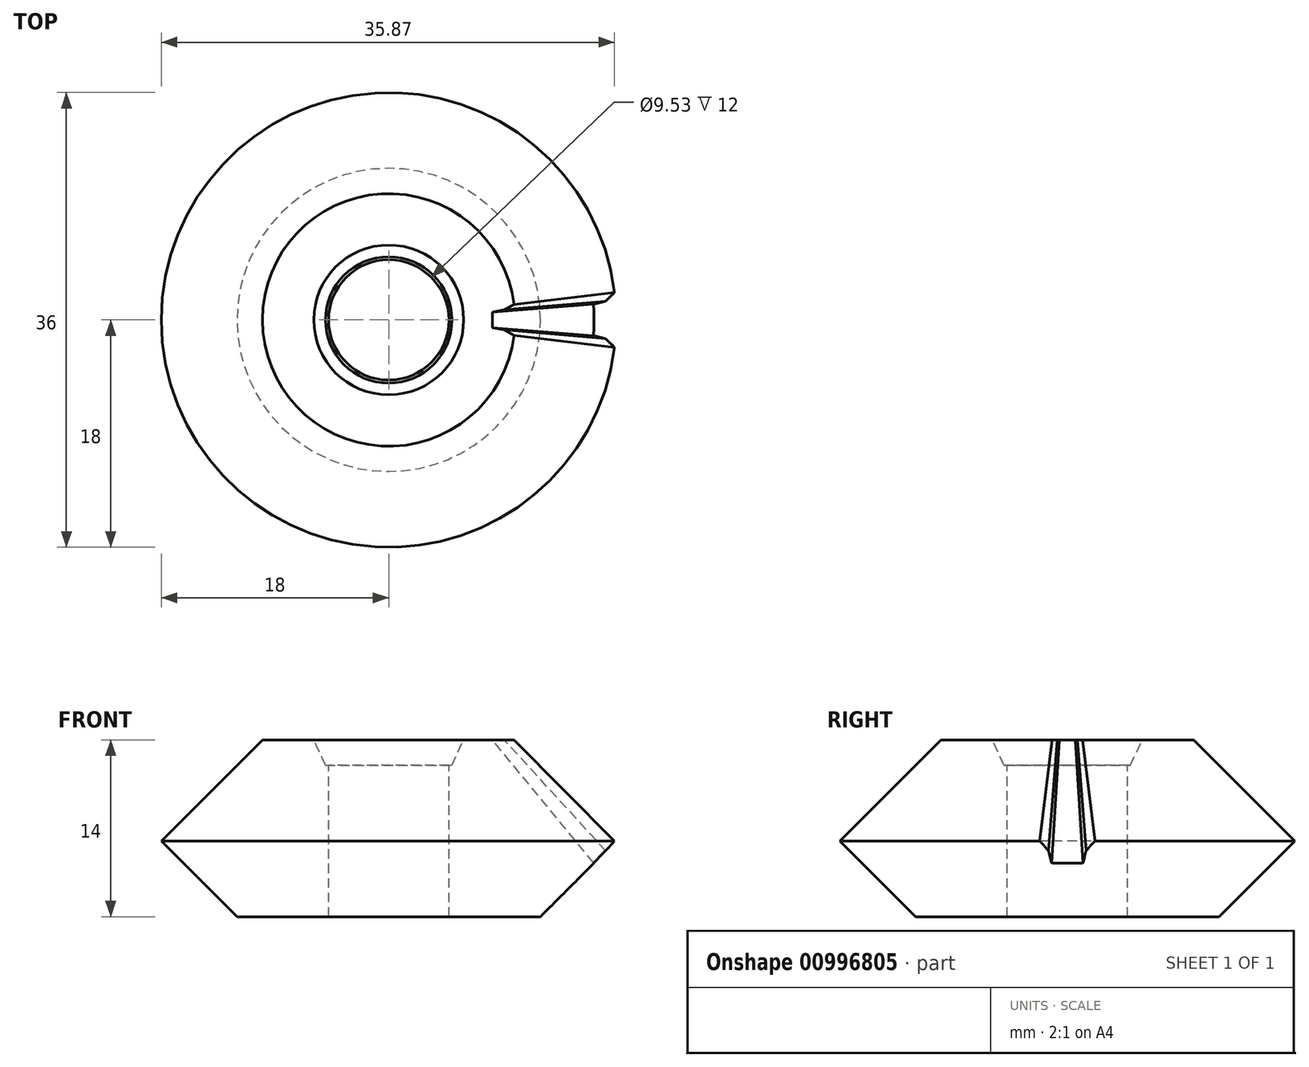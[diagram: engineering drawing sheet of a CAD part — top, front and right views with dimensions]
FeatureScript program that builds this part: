
annotation { "Feature Type Name" : "Feature", "Feature Type Description" : "" }
export const myFeature = defineFeature(function(context is Context, id is Id, definition is map)
    precondition{}
    {
        {
            var Q0;
            Q0=qCreatedBy(makeId("Front.planeOp"),FACE);
            var sketch = newSketch(context, id + "F0", { "sketchPlane" : qUnion([Q0])});
            skLineSegment(sketch, "E0", {"start": v(18, 6) * mm, "end": v(0, 24) * mm});
            skLineSegment(sketch, "E1", {"start": v(0, 24) * mm, "end": v(0, 0) * mm});
            skLineSegment(sketch, "E2", {"start": v(0, 0) * mm, "end": v(12, 0) * mm});
            skLineSegment(sketch, "E3", {"start": v(12, 0) * mm, "end": v(18, 6) * mm});
            skSolve(sketch);
        }
        {
            var Q0;
            Q0=makeQuery(id+"F0.imprint","IMPRINT",FACE,{"disambiguationData":[TD([[makeQuery(id+"F0.imprint","IMPRINT",EDGE,{"derivedFrom":sQuery(id+"F0.wireOp",EDGE,"iZfwdum0-eERQ-opZv-YKFB-7AKXDabp0p0H")}),1.0]])]});
            var Q1;
            Q1=makeQuery(id+"F0.imprint","IMPRINT",FACE,{"disambiguationData":[TD([[makeQuery(id+"F0.imprint","IMPRINT",EDGE,{"derivedFrom":sQuery(id+"F0.wireOp",EDGE,"E0")}),1.0]])]});
            var Q2;
            Q2=sQuery(id+"F0.wireOp",EDGE,"E1");
            revolve(context, id + "F1", {"surfaceOperationType" : NewSurfaceOperationType.NEW, "entities" : qUnion([Q0, Q1]), "axis" : qUnion([Q2]), "revolveType" : RevolveType.FULL});
        }
        {
            var Q0;
            Q0=sQuery(id+"F0.wireOp",EDGE,"E0");
            var Q1;
            Q1=sQuery(id+"F0.wireOp",VERTEX,"E0.start");
            cPlane(context, id + "F2", {"entities" : qUnion([Q0, Q1]), "cplaneType" : CPlaneType.LINE_POINT, "offset" : 25 * mm, "width" : 150 * mm, "height" : 150 * mm});
        }
        {
            var Q0;
            Q0=qCreatedBy(id+"F2.planeOp",FACE);
            var sketch = newSketch(context, id + "F3", { "sketchPlane" : qUnion([Q0])});
            skPoint(sketch, "E4.0", {"position": v(0, 16.97) * mm});
            skLineSegment(sketch, "E5", {"start": v(0, 0) * mm, "end": v(-4.6, 29.03) * mm, "construction": true});
            skLineSegment(sketch, "E6", {"start": v(0, 0) * mm, "end": v(0, 16.97) * mm, "construction": true});
            skLineSegment(sketch, "E7", {"start": v(0, 14.47) * mm, "end": v(-1.25, 14.47) * mm});
            skLineSegment(sketch, "E8", {"start": v(-1.25, 14.47) * mm, "end": v(-1.49, 15.83) * mm});
            skLineSegment(sketch, "E9", {"start": v(-1.49, 15.83) * mm, "end": v(-2.25, 16.97) * mm});
            skLineSegment(sketch, "E10", {"start": v(-1.25, 14.47) * mm, "end": v(-2.25, 16.97) * mm, "construction": true});
            skLineSegment(sketch, "E11", {"start": v(-1.49, 15.83) * mm, "end": v(-1.75, 15.72) * mm, "construction": true});
            skLineSegment(sketch, "E12.MirrorCS", {"start": v(0, 14.47) * mm, "end": v(1.25, 14.47) * mm});
            skLineSegment(sketch, "E13.MirrorCS", {"start": v(1.25, 14.47) * mm, "end": v(1.49, 15.83) * mm});
            skLineSegment(sketch, "E14.MirrorCS", {"start": v(1.49, 15.83) * mm, "end": v(2.25, 16.97) * mm});
            skLineSegment(sketch, "E15", {"start": v(2.25, 16.97) * mm, "end": v(-2.25, 16.97) * mm});
            skSolve(sketch);
        }
        {
            var Q0;
            Q0=makeQuery(id+"F3.imprint","IMPRINT",FACE,{"disambiguationData":[TD([[makeQuery(id+"F3.imprint","IMPRINT",EDGE,{"derivedFrom":sQuery(id+"F3.wireOp",EDGE,"E7")}),-1.0]])]});
            var Q1;
            Q1=makeQuery(id+"F1.opRevolve","SWEPT_VERTEX",VERTEX,{"disambiguationData":[OSD([sQuery(id+"F0.wireOp",EDGE,"E0"),sQuery(id+"F0.wireOp",EDGE,"E1")])]});
            loft(context, id + "F4", {"operationType" : NewBodyOperationType.REMOVE, "sheetProfilesArray" : [{ "sheetProfileEntities" : qUnion([Q0]) }, { "sheetProfileEntities" : qUnion([Q1]) }]});
        }
        {
            var Q0;
            Q0=qCreatedBy(makeId("Front.planeOp"),FACE);
            var sketch = newSketch(context, id + "F5", { "sketchPlane" : qUnion([Q0])});
            skPoint(sketch, "E16.0", {"position": v(0, 24) * mm});
            skLineSegment(sketch, "E17", {"start": v(0, 24) * mm, "end": v(0, 12) * mm});
            skLineSegment(sketch, "E18", {"start": v(0, 12) * mm, "end": v(5, 12) * mm});
            skLineSegment(sketch, "E19", {"start": v(5, 12) * mm, "end": v(5.93, 14) * mm});
            skLineSegment(sketch, "E20", {"start": v(5.93, 14) * mm, "end": v(21.55, 14) * mm});
            skLineSegment(sketch, "E21", {"start": v(21.55, 14) * mm, "end": v(0, 24) * mm});
            skSolve(sketch);
        }
        {
            var Q0;
            Q0=makeQuery(id+"F5.imprint","IMPRINT",FACE,{"disambiguationData":[TD([[makeQuery(id+"F5.imprint","IMPRINT",EDGE,{"derivedFrom":sQuery(id+"F5.wireOp",EDGE,"E17")}),1.0]])]});
            var Q1;
            Q1=sQuery(id+"F5.wireOp",EDGE,"E17");
            revolve(context, id + "F6", {"operationType" : NewBodyOperationType.REMOVE, "surfaceOperationType" : NewSurfaceOperationType.NEW, "entities" : qUnion([Q0]), "axis" : qUnion([Q1]), "revolveType" : RevolveType.FULL, "oppositeDirection" : true});
        }
        {
            var Q0;
            Q0=makeQuery(id+"F6.boolean.opBoolean","COPY",FACE,{"derivedFrom":makeQuery(id+"F6.opRevolve","SWEPT_FACE",FACE,{"disambiguationData":[OSD([sQuery(id+"F5.wireOp",EDGE,"E18")])]})});
            var sketch = newSketch(context, id + "F7", { "sketchPlane" : qUnion([Q0])});
            skCircle(sketch, "E22", {"center": v(0, 0) * mm, "radius": 4.76 * mm});
            skSolve(sketch);
        }
        {
            var Q0;
            Q0 = qSketchRegion(id + "F7", true);
            extrude(context, id + "F8", {"entities" : qUnion([Q0]), "operationType" : NewBodyOperationType.REMOVE, "endBound" : BoundingType.THROUGH_ALL, "oppositeDirection" : true, "depth" : 25 * mm, "offsetDistance" : 25 * mm});
        }
    });
